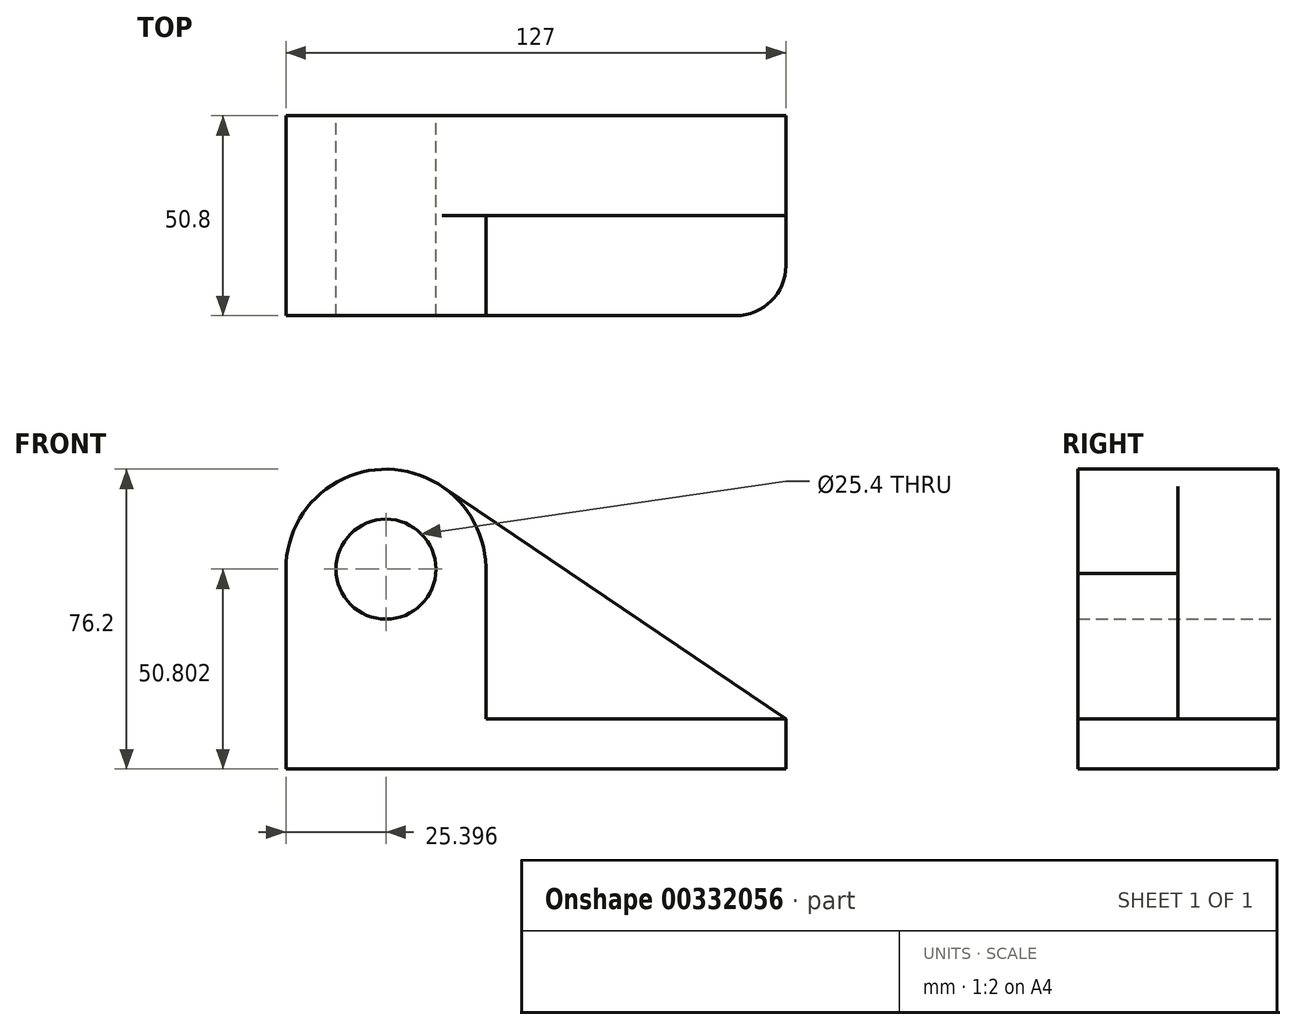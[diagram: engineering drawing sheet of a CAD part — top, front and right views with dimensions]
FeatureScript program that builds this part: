
annotation { "Feature Type Name" : "Feature", "Feature Type Description" : "" }
export const myFeature = defineFeature(function(context is Context, id is Id, definition is map)
    precondition{}
    {
        {
            var Q0;
            Q0=qCreatedBy(makeId("Front.planeOp"),FACE);
            var sketch = newSketch(context, id + "F0", { "sketchPlane" : qUnion([Q0])});
            skCircle(sketch, "E0", {"center": v(-40.23, 35.71) * mm, "radius": 12.7 * mm});
            skArc(sketch, "E1", {"start": v(-26, 56.75) * mm, "mid": v(-52.14, 58.15) * mm, "end": v(-65.63, 35.71) * mm});
            skLineSegment(sketch, "E2", {"start": v(-65.63, 35.71) * mm, "end": v(-65.63, -15.09) * mm});
            skLineSegment(sketch, "E3", {"start": v(-65.63, -15.09) * mm, "end": v(61.37, -15.09) * mm});
            skLineSegment(sketch, "E4", {"start": v(61.37, -15.09) * mm, "end": v(61.37, -2.39) * mm});
            skLineSegment(sketch, "E5", {"start": v(61.37, -2.39) * mm, "end": v(-26, 56.75) * mm});
            skSolve(sketch);
        }
        {
            var Q0;
            Q0=makeQuery(id+"F0.imprint","IMPRINT",FACE,{"disambiguationData":[TD([[makeQuery(id+"F0.imprint","IMPRINT",EDGE,{"derivedFrom":sQuery(id+"F0.wireOp",EDGE,"E0")}),-1.0]])]});
            extrude(context, id + "F1", {"entities" : qUnion([Q0]), "depth" : 25.4 * mm});
        }
        {
            var Q0;
            Q0=makeQuery(id+"F1.opExtrude","CAP_FACE",FACE,{"disambiguationData":[OSD([sQuery(id+"F0.wireOp",EDGE,"E0"),sQuery(id+"F0.wireOp",EDGE,"E1"),sQuery(id+"F0.wireOp",EDGE,"E2"),sQuery(id+"F0.wireOp",EDGE,"E3"),sQuery(id+"F0.wireOp",EDGE,"E4"),sQuery(id+"F0.wireOp",EDGE,"E5")])],"isStart":false});
            var sketch = newSketch(context, id + "F2", { "sketchPlane" : qUnion([Q0])});
            skCircle(sketch, "E6", {"center": v(-40.23, 35.71) * mm, "radius": 12.7 * mm});
            skCircle(sketch, "E7", {"center": v(-40.23, 35.71) * mm, "radius": 25.4 * mm});
            skLineSegment(sketch, "E8.bottom", {"start": v(61.37, -2.39) * mm, "end": v(-14.8, -2.39) * mm});
            skLineSegment(sketch, "E8.top", {"start": v(61.37, -15.09) * mm, "end": v(-65.63, -15.09) * mm});
            skLineSegment(sketch, "E8.left", {"start": v(61.37, -2.39) * mm, "end": v(61.37, -15.09) * mm});
            skLineSegment(sketch, "E8.right", {"start": v(-65.63, -2.39) * mm, "end": v(-65.63, -15.09) * mm});
            skLineSegment(sketch, "E9", {"start": v(-14.86, 34.6) * mm, "end": v(-14.8, -2.39) * mm});
            skSolve(sketch);
        }
        {
            var Q0;
            Q0=makeQuery(id+"F2.imprint","IMPRINT",FACE,{"disambiguationData":[TD([[makeQuery(id+"F2.imprint","IMPRINT",EDGE,{"derivedFrom":sQuery(id+"F2.wireOp",EDGE,"E8.bottom")}),1.0]])]});
            var Q1;
            Q1=makeQuery(id+"F2.imprint","IMPRINT",FACE,{"disambiguationData":[TD([[makeQuery(id+"F2.imprint","IMPRINT",EDGE,{"derivedFrom":sQuery(id+"F2.wireOp",EDGE,"E6")}),-1.0]])]});
            extrude(context, id + "F3", {"entities" : qUnion([Q0, Q1]), "operationType" : NewBodyOperationType.ADD, "depth" : 25.4 * mm});
        }
        {
            var Q0;
            Q0=makeQuery(id+"F3.opExtrude","CAP_EDGE",EDGE,{"disambiguationData":[OSD([sQuery(id+"F2.wireOp",EDGE,"E8.left")])],"isStart":false});
            fillet(context, id + "F4", {"entities" : qUnion([Q0]), "radius" : 12.7 * mm, "tangentPropagation" : true, "allowEdgeOverflow" : false});
        }
    });
